# Revit family: Modular_Desks-Teknion-RDRR_Rectangular_Desk_Full_Gables-R2019
name_source: partatom
category: Furniture
units: mm (PartAtom-declared; Revit-internal decimal feet)

## family parameters
Always vertical = Yes
Cut with Voids When Loaded = No
OmniClass Number = 23.40.20.00
OmniClass Title = General Furniture and Specialties
Room Calculation Point = No
Shared = Yes
Work Plane-Based = No

## types (10) — shared parameters
Assembly Code = E2020200
Manufacturer = Teknion
Manufacturer Fax = 416.661.4586
Part Number = RDRR
Product Documentation Link = https://www.teknion.com
Product Line = Expansion Desking
Product Page URL = https://www.teknion.com
Series = Expansion Desking
Sustainability Data = https://www.teknion.com
URL = www.teknion.com
Unit Weight URL = http://www.teknion.com
Warranty = http://www.teknion.com

## per-type parameters (varying)
| type | Back Leg Offset | Depth | Description | Gabel and Grommet Finish Note | Gable and Grommet Finish | Laminate | Metal C Leg | Metal C Leg Cut Depth | Metal Gable | Metal/Laminate Gable 2D | Model |
| Metal Gable Style, 24" Depth | 1.459 " | 24 " | Rectangular Desk – Full Gables, Metal Gable Style, 24" Depth | Please choose a Foundation or MIca Paint Finish | Paint - Teknion - Mica - Platinum | No | No | 0.5 " | Yes | Yes | RDRRM24__ |
| Metal Gable Style, 20" Depth | 1.459 " | 20 " | Rectangular Desk – Full Gables, Metal Gable Style, 20" Depth | Please choose a Foundation or MIca Paint Finish | Paint - Teknion - Mica - Platinum | No | No | 0.5 " | Yes | Yes | RDRRM20__ |
| Metal Gable Style, 30" Depth | 1.459 " | 30 " | Rectangular Desk – Full Gables, Metal Gable Style, 30" Depth | Please choose a Foundation or MIca Paint Finish | Paint - Teknion - Mica - Platinum | No | No | 0.5 " | Yes | Yes | RDRRM30__ |
| Metal Gable Style, 36" Depth | 1.459 " | 36 " | Rectangular Desk – Full Gables, Metal Gable Style, 36" Depth | Please choose a Foundation or MIca Paint Finish | Paint - Teknion - Mica - Platinum | No | No | 0.5 " | Yes | Yes | RDRRM36__ |
| Metal C-Leg, 24" Depth | 1.459 " | 24 " | Rectangular Desk – Full Gables, Metal C-Leg Style, 24" Depth | Please choose a Foundation or MIca Paint Finish | Paint - Teknion - Mica - Platinum | No | Yes | 96 " | No | No | RDRRC24__ |
| Metal C-Leg, 30" Depth | 7.553 " | 30 " | Rectangular Desk – Full Gables, Metal C-Leg Style, 30" Depth | Please choose a Foundation or MIca Paint Finish | Paint - Teknion - Mica - Platinum | No | Yes | 96 " | No | No | RDRRC30__ |
| Laminate Gable Style, 20" Depth | 1.459 " | 20 " | Rectangular Desk – Full Gables, Laminate Gable Style, 20" Depth | Please choose a Source Laminate Finish. | Laminate - Teknion - 2L - Coastal Elm | Yes | No | 0.5 " | No | Yes | RDRRL20__ |
| Laminate Gable Style, 24" Depth | 1.459 " | 24 " | Rectangular Desk – Full Gables, Laminate Gable Style, 24" Depth | Please choose a Source Laminate Finish. | Laminate - Teknion - 2L - Coastal Elm | Yes | No | 0.5 " | No | Yes | RDRRL24__ |
| Laminate Gable Style, 30" Depth | 1.459 " | 30 " | Rectangular Desk – Full Gables, Laminate Gable Style, 30" Depth | Please choose a Source Laminate Finish. | Laminate - Teknion - 2L - Coastal Elm | Yes | No | 0.5 " | No | Yes | RDRRL30__ |
| Laminate Gable Style, 36" Depth | 1.459 " | 36 " | Rectangular Desk – Full Gables, Laminate Gable Style, 36" Depth | Please choose a Source Laminate Finish. | Laminate - Teknion - 2L - Coastal Elm | Yes | No | 0.5 " | No | Yes | RDRRL36__ |

## geometry (parser evidence)
native form markers: Sweep x3
no freeform markers — native parametric forms only
